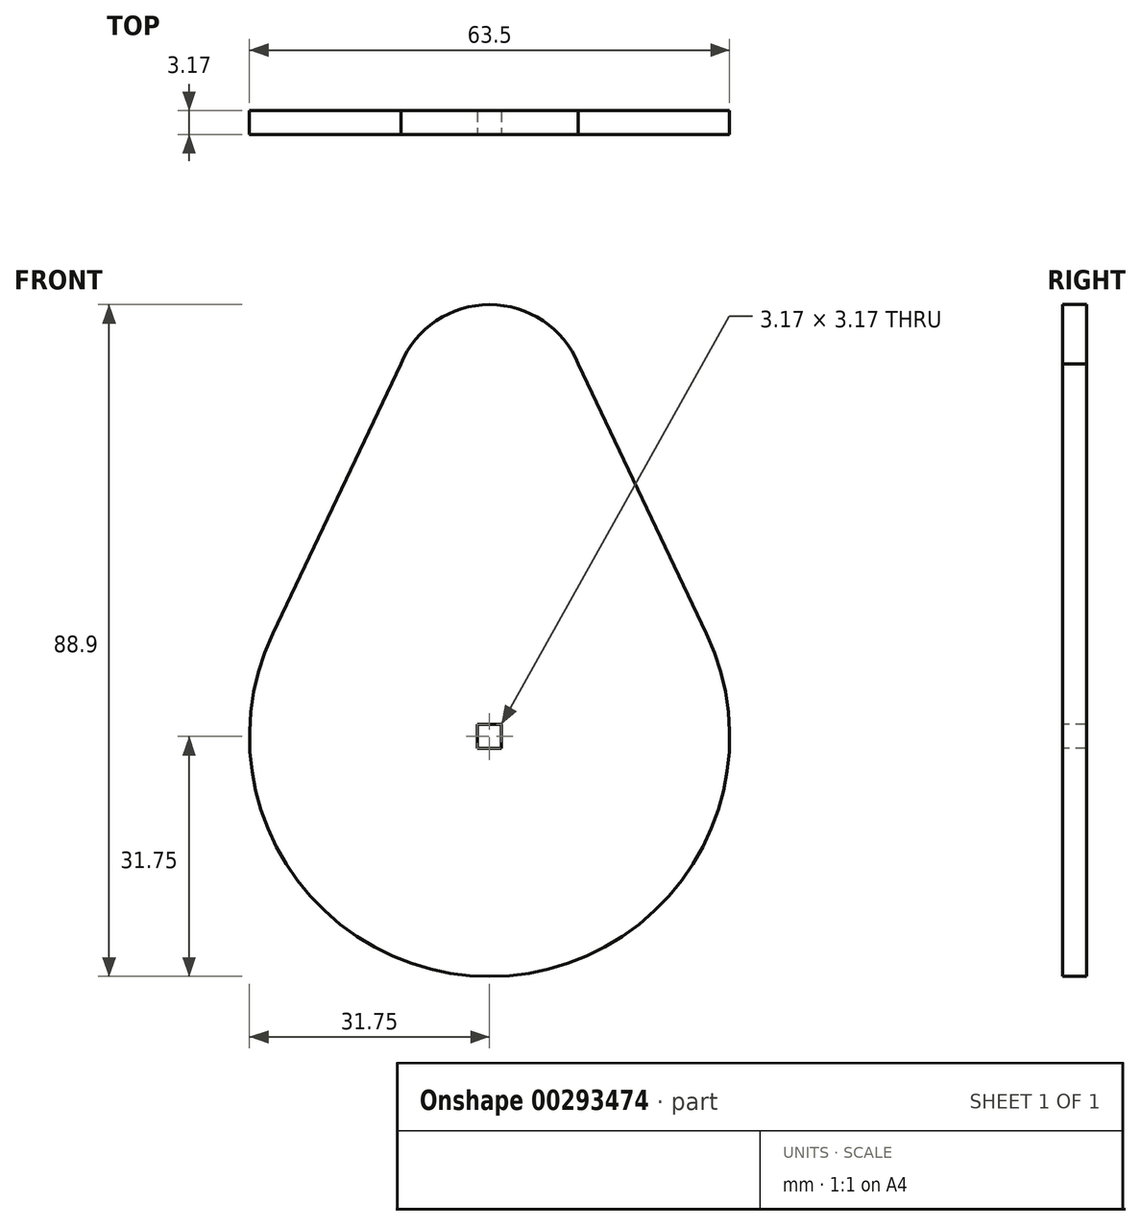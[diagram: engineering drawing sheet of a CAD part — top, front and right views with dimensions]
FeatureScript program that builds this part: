
annotation { "Feature Type Name" : "Feature", "Feature Type Description" : "" }
export const myFeature = defineFeature(function(context is Context, id is Id, definition is map)
    precondition{}
    {
        {
            var Q0;
            Q0=qCreatedBy(makeId("Front.planeOp"),FACE);
            var sketch = newSketch(context, id + "F0", { "sketchPlane" : qUnion([Q0])});
            skCircle(sketch, "E0", {"center": v(0, 0) * mm, "radius": 31.75 * mm});
            skLineSegment(sketch, "E1", {"start": v(0, 0) * mm, "end": v(0, 44.45) * mm});
            skCircle(sketch, "E2", {"center": v(0, 44.45) * mm, "radius": 12.7 * mm});
            skLineSegment(sketch, "E3", {"start": v(-11.17, 50.5) * mm, "end": v(-28.68, 13.62) * mm});
            skLineSegment(sketch, "E4", {"start": v(-11.17, 50.5) * mm, "end": v(11.17, 50.5) * mm});
            skLineSegment(sketch, "E5", {"start": v(11.17, 50.5) * mm, "end": v(28.68, 13.62) * mm});
            skSolve(sketch);
        }
        {
            var Q0;
            {var subQ0=sQuery(id+"F0.wireOp",EDGE,"E5");var subQ1=sQuery(id+"F0.wireOp",EDGE,"E2");var subQ3=makeQuery(id+"F0.imprint","INTERSECT",VERTEX,{"derivedFrom":[subQ1,subQ0]});Q0=makeQuery(id+"F0.imprint","IMPRINT",FACE,{"disambiguationData":[TD([[makeQuery(id+"F0.imprint","IMPRINT",EDGE,{"disambiguationData":[TD([[subQ3,-1.0]])],"derivedFrom":subQ1}),1.0]])]});}
            var Q1;
            {var subQ0=sQuery(id+"F0.wireOp",EDGE,"E4");Q1=makeQuery(id+"F0.imprint","IMPRINT",FACE,{"disambiguationData":[TD([[makeQuery(id+"F0.imprint","IMPRINT",EDGE,{"derivedFrom":subQ0}),1.0]])]});}
            var Q2;
            {var subQ0=sQuery(id+"F0.wireOp",EDGE,"E3");var subQ1=sQuery(id+"F0.wireOp",EDGE,"E2");var subQ3=makeQuery(id+"F0.imprint","INTERSECT",VERTEX,{"derivedFrom":[subQ1,subQ0]});Q2=makeQuery(id+"F0.imprint","IMPRINT",FACE,{"disambiguationData":[TD([[makeQuery(id+"F0.imprint","IMPRINT",EDGE,{"disambiguationData":[TD([[subQ3,1.0]])],"derivedFrom":subQ1}),1.0]])]});}
            var Q3;
            {var subQ0=sQuery(id+"F0.wireOp",EDGE,"E5");var subQ1=sQuery(id+"F0.wireOp",EDGE,"E0");var subQ2=makeQuery(id+"F0.imprint","INTERSECT",VERTEX,{"derivedFrom":[subQ1,subQ0]});Q3=makeQuery(id+"F0.imprint","IMPRINT",FACE,{"disambiguationData":[TD([[makeQuery(id+"F0.imprint","IMPRINT",EDGE,{"disambiguationData":[TD([[subQ2,-1.0]])],"derivedFrom":subQ1}),-1.0]])]});}
            var Q4;
            {var subQ0=sQuery(id+"F0.wireOp",EDGE,"E3");var subQ1=sQuery(id+"F0.wireOp",EDGE,"E0");var subQ2=makeQuery(id+"F0.imprint","INTERSECT",VERTEX,{"derivedFrom":[subQ1,subQ0]});Q4=makeQuery(id+"F0.imprint","IMPRINT",FACE,{"disambiguationData":[TD([[makeQuery(id+"F0.imprint","IMPRINT",EDGE,{"disambiguationData":[TD([[subQ2,1.0]])],"derivedFrom":subQ1}),-1.0]])]});}
            var Q5;
            {var subQ0=sQuery(id+"F0.wireOp",EDGE,"E4");Q5=makeQuery(id+"F0.imprint","IMPRINT",FACE,{"disambiguationData":[TD([[makeQuery(id+"F0.imprint","IMPRINT",EDGE,{"derivedFrom":subQ0}),-1.0]])]});}
            var Q6;
            {var subQ0=sQuery(id+"F0.wireOp",EDGE,"E0");var subQ1=makeQuery(id+"F0.imprint","INTERSECT",VERTEX,{"derivedFrom":[subQ0,sQuery(id+"F0.wireOp",EDGE,"E5")]});Q6=makeQuery(id+"F0.imprint","IMPRINT",FACE,{"disambiguationData":[TD([[makeQuery(id+"F0.imprint","IMPRINT",EDGE,{"disambiguationData":[TD([[subQ1,-1.0]])],"derivedFrom":subQ0}),1.0]])]});}
            extrude(context, id + "F1", {"entities" : qUnion([Q0, Q1, Q2, Q3, Q4, Q5, Q6]), "depth" : 3.17 * mm});
        }
        {
            var Q0;
            Q0=makeQuery(id+"F1.opExtrude","CAP_FACE",FACE,{"disambiguationData":[OSD([sQuery(id+"F0.wireOp",EDGE,"E0"),sQuery(id+"F0.wireOp",EDGE,"E2"),sQuery(id+"F0.wireOp",EDGE,"E3"),sQuery(id+"F0.wireOp",EDGE,"E5")])],"isStart":false});
            var sketch = newSketch(context, id + "F2", { "sketchPlane" : qUnion([Q0])});
            skLineSegment(sketch, "E6.bottom", {"start": v(1.59, 1.59) * mm, "end": v(-1.59, 1.59) * mm});
            skLineSegment(sketch, "E6.top", {"start": v(1.59, -1.59) * mm, "end": v(-1.59, -1.59) * mm});
            skLineSegment(sketch, "E6.left", {"start": v(1.59, 1.59) * mm, "end": v(1.59, -1.59) * mm});
            skLineSegment(sketch, "E6.right", {"start": v(-1.59, 1.59) * mm, "end": v(-1.59, -1.59) * mm});
            skPoint(sketch, "E6.middle", {"position": v(0, 0) * mm});
            skSolve(sketch);
        }
        {
            var Q0;
            Q0=makeQuery(id+"F2.imprint","IMPRINT",FACE,{"disambiguationData":[TD([[makeQuery(id+"F2.imprint","IMPRINT",EDGE,{"derivedFrom":sQuery(id+"F2.wireOp",EDGE,"E6.bottom")}),1.0]])]});
            extrude(context, id + "F3", {"entities" : qUnion([Q0]), "operationType" : NewBodyOperationType.REMOVE, "endBound" : BoundingType.THROUGH_ALL, "oppositeDirection" : true, "depth" : 25.4 * mm});
        }
    });
